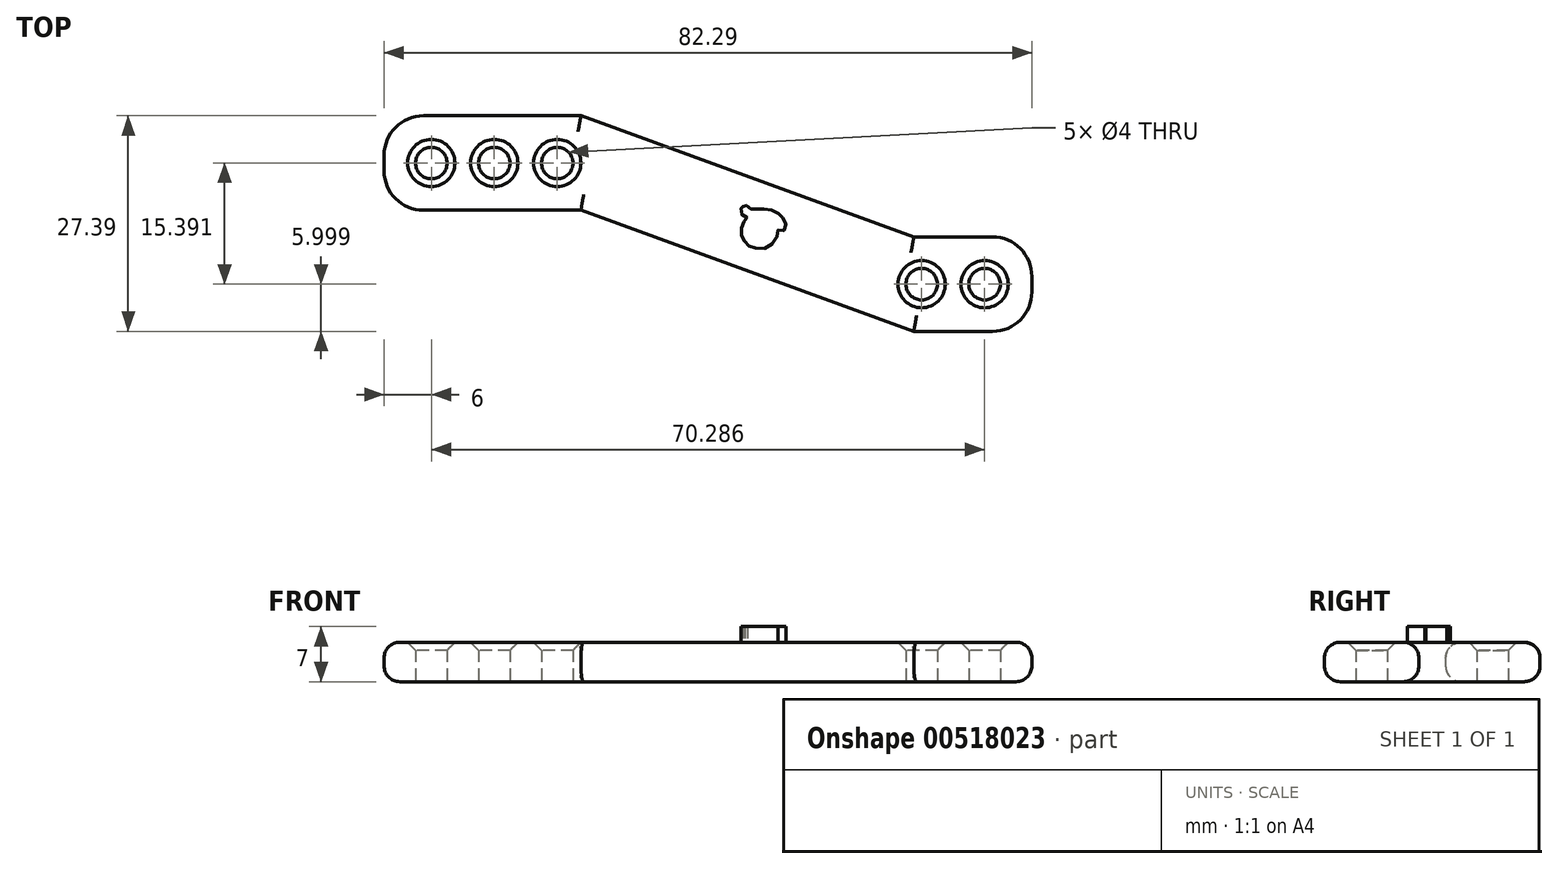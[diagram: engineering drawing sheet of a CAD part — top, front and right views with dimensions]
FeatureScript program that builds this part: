
annotation { "Feature Type Name" : "Feature", "Feature Type Description" : "" }
export const myFeature = defineFeature(function(context is Context, id is Id, definition is map)
    precondition{}
    {
        {
            var Q0;
            Q0=qCreatedBy(makeId("Top.planeOp"),FACE);
            var sketch = newSketch(context, id + "F0", { "sketchPlane" : qUnion([Q0])});
            skLineSegment(sketch, "E0.bottom", {"start": v(0, 0) * mm, "end": v(25, 0) * mm});
            skLineSegment(sketch, "E0.top", {"start": v(0, -12) * mm, "end": v(25, -12) * mm});
            skLineSegment(sketch, "E0.left", {"start": v(0, 0) * mm, "end": v(0, -12) * mm});
            skLineSegment(sketch, "E0.right", {"start": v(25, 0) * mm, "end": v(25, -12) * mm});
            skLineSegment(sketch, "E1", {"start": v(25, -12) * mm, "end": v(67.29, -27.4) * mm});
            skLineSegment(sketch, "E2", {"start": v(25, 0) * mm, "end": v(67.29, -15.4) * mm});
            skLineSegment(sketch, "E3", {"start": v(67.29, -15.4) * mm, "end": v(67.29, -27.4) * mm});
            skLineSegment(sketch, "E4.bottom", {"start": v(67.29, -27.4) * mm, "end": v(67.29, -27.4) * mm});
            skLineSegment(sketch, "E4.top", {"start": v(67.29, -15.4) * mm, "end": v(67.29, -15.4) * mm});
            skLineSegment(sketch, "E4.left", {"start": v(67.29, -27.4) * mm, "end": v(67.29, -15.4) * mm});
            skLineSegment(sketch, "E4.right", {"start": v(67.29, -27.4) * mm, "end": v(67.29, -15.4) * mm});
            skLineSegment(sketch, "E5.bottom", {"start": v(67.29, -27.4) * mm, "end": v(82.29, -27.4) * mm});
            skLineSegment(sketch, "E5.top", {"start": v(67.29, -15.4) * mm, "end": v(82.29, -15.4) * mm});
            skLineSegment(sketch, "E5.right", {"start": v(82.29, -27.4) * mm, "end": v(82.29, -15.4) * mm});
            skSolve(sketch);
        }
        {
            var Q0;
            Q0 = qSketchRegion(id + "F0", true);
            extrude(context, id + "F1", {"entities" : qUnion([Q0]), "depth" : 5 * mm, "offsetDistance" : 25 * mm});
        }
        {
            var Q0;
            Q0=qCreatedBy(makeId("Top.planeOp"),FACE);
            var sketch = newSketch(context, id + "F2", { "sketchPlane" : qUnion([Q0])});
            skCircle(sketch, "E6", {"center": v(6, -6) * mm, "radius": 2 * mm});
            skCircle(sketch, "E7", {"center": v(76.29, -21.4) * mm, "radius": 2 * mm});
            skCircle(sketch, "E8.1.0.0", {"center": v(14, -6) * mm, "radius": 2 * mm});
            skCircle(sketch, "E8.2.0.0", {"center": v(22, -6) * mm, "radius": 2 * mm});
            skLineSegment(sketch, "E8.direction1", {"start": v(6, -6) * mm, "end": v(14, -6) * mm, "construction": true});
            skCircle(sketch, "E9.1.0.0", {"center": v(68.29, -21.4) * mm, "radius": 2 * mm});
            skLineSegment(sketch, "E9.direction1", {"start": v(76.29, -21.4) * mm, "end": v(68.29, -21.4) * mm, "construction": true});
            skSolve(sketch);
        }
        {
            var Q0;
            Q0 = qSketchRegion(id + "F2", true);
            extrude(context, id + "F3", {"entities" : qUnion([Q0]), "operationType" : NewBodyOperationType.REMOVE, "endBound" : BoundingType.THROUGH_ALL, "depth" : 25 * mm, "offsetDistance" : 25 * mm});
        }
        {
            var Q0;
            Q0=makeQuery(id+"F1.opExtrude","CAP_EDGE",EDGE,{"disambiguationData":[OSD([sQuery(id+"F0.wireOp",EDGE,"E0.top")])],"isStart":false});
            var Q1;
            Q1=makeQuery(id+"F1.opExtrude","CAP_EDGE",EDGE,{"disambiguationData":[OSD([sQuery(id+"F0.wireOp",EDGE,"E2")])],"isStart":false});
            var Q2;
            Q2=makeQuery(id+"F1.opExtrude","CAP_EDGE",EDGE,{"disambiguationData":[OSD([sQuery(id+"F0.wireOp",EDGE,"E1")])],"isStart":false});
            var Q3;
            Q3=makeQuery(id+"F1.opExtrude","CAP_EDGE",EDGE,{"disambiguationData":[OSD([sQuery(id+"F0.wireOp",EDGE,"E5.top")])],"isStart":false});
            var Q4;
            Q4=makeQuery(id+"F1.opExtrude","CAP_EDGE",EDGE,{"disambiguationData":[OSD([sQuery(id+"F0.wireOp",EDGE,"E5.right")])],"isStart":false});
            var Q5;
            Q5=makeQuery(id+"F1.opExtrude","CAP_EDGE",EDGE,{"disambiguationData":[OSD([sQuery(id+"F0.wireOp",EDGE,"E5.bottom")])],"isStart":false});
            var Q6;
            Q6=makeQuery(id+"F1.opExtrude","CAP_EDGE",EDGE,{"disambiguationData":[OSD([sQuery(id+"F0.wireOp",EDGE,"E0.bottom")])],"isStart":false});
            var Q7;
            Q7=makeQuery(id+"F1.opExtrude","CAP_EDGE",EDGE,{"disambiguationData":[OSD([sQuery(id+"F0.wireOp",EDGE,"E0.left")])],"isStart":false});
            var Q8;
            Q8=makeQuery(id+"F1.opExtrude","CAP_EDGE",EDGE,{"disambiguationData":[OSD([sQuery(id+"F0.wireOp",EDGE,"E5.right")])],"isStart":true});
            var Q9;
            Q9=makeQuery(id+"F1.opExtrude","CAP_EDGE",EDGE,{"disambiguationData":[OSD([sQuery(id+"F0.wireOp",EDGE,"E5.top")])],"isStart":true});
            var Q10;
            Q10=makeQuery(id+"F1.opExtrude","CAP_EDGE",EDGE,{"disambiguationData":[OSD([sQuery(id+"F0.wireOp",EDGE,"E2")])],"isStart":true});
            var Q11;
            Q11=makeQuery(id+"F1.opExtrude","CAP_EDGE",EDGE,{"disambiguationData":[OSD([sQuery(id+"F0.wireOp",EDGE,"E0.bottom")])],"isStart":true});
            var Q12;
            Q12=makeQuery(id+"F1.opExtrude","CAP_EDGE",EDGE,{"disambiguationData":[OSD([sQuery(id+"F0.wireOp",EDGE,"E0.left")])],"isStart":true});
            var Q13;
            Q13=makeQuery(id+"F1.opExtrude","CAP_EDGE",EDGE,{"disambiguationData":[OSD([sQuery(id+"F0.wireOp",EDGE,"E0.top")])],"isStart":true});
            var Q14;
            Q14=makeQuery(id+"F1.opExtrude","CAP_EDGE",EDGE,{"disambiguationData":[OSD([sQuery(id+"F0.wireOp",EDGE,"E1")])],"isStart":true});
            var Q15;
            Q15=makeQuery(id+"F1.opExtrude","CAP_EDGE",EDGE,{"disambiguationData":[OSD([sQuery(id+"F0.wireOp",EDGE,"E5.bottom")])],"isStart":true});
            fillet(context, id + "F4", {"entities" : qUnion([Q0, Q1, Q2, Q3, Q4, Q5, Q6, Q7, Q8, Q9, Q10, Q11, Q12, Q13, Q14, Q15]), "radius" : 2 * mm, "tangentPropagation" : true, "allowEdgeOverflow" : false});
        }
        {
            var Q0;
            Q0=makeQuery(id+"F1.opExtrude","SWEPT_EDGE",EDGE,{"disambiguationData":[OSD([sQuery(id+"F0.wireOp",EDGE,"E0.top"),sQuery(id+"F0.wireOp",EDGE,"E0.left")])]});
            var Q1;
            Q1=makeQuery(id+"F1.opExtrude","SWEPT_EDGE",EDGE,{"disambiguationData":[OSD([sQuery(id+"F0.wireOp",EDGE,"E0.bottom"),sQuery(id+"F0.wireOp",EDGE,"E0.left")])]});
            var Q2;
            Q2=makeQuery(id+"F1.opExtrude","SWEPT_EDGE",EDGE,{"disambiguationData":[OSD([sQuery(id+"F0.wireOp",EDGE,"E5.top"),sQuery(id+"F0.wireOp",EDGE,"E5.right")])]});
            var Q3;
            Q3=makeQuery(id+"F1.opExtrude","SWEPT_EDGE",EDGE,{"disambiguationData":[OSD([sQuery(id+"F0.wireOp",EDGE,"E5.bottom"),sQuery(id+"F0.wireOp",EDGE,"E5.right")])]});
            fillet(context, id + "F5", {"entities" : qUnion([Q0, Q1, Q2, Q3]), "radius" : 5 * mm, "tangentPropagation" : true, "allowEdgeOverflow" : false});
        }
        {
            var Q0;
            Q0=makeQuery(id+"F3.boolean.opBoolean","INTERSECT",EDGE,{"derivedFrom":[makeQuery(id+"F1.opExtrude","CAP_FACE",FACE,{"disambiguationData":[OSD([sQuery(id+"F0.wireOp",EDGE,"E0.bottom"),sQuery(id+"F0.wireOp",EDGE,"E0.top"),sQuery(id+"F0.wireOp",EDGE,"E0.left"),sQuery(id+"F0.wireOp",EDGE,"E1"),sQuery(id+"F0.wireOp",EDGE,"E2"),sQuery(id+"F0.wireOp",EDGE,"E5.bottom"),sQuery(id+"F0.wireOp",EDGE,"E5.top"),sQuery(id+"F0.wireOp",EDGE,"E5.right")])],"isStart":false}),makeQuery(id+"F3.opExtrude","SWEPT_FACE",FACE,{"disambiguationData":[OSD([sQuery(id+"F2.wireOp",EDGE,"E9.1.0.0")])]})]});
            var Q1;
            Q1=makeQuery(id+"F3.boolean.opBoolean","INTERSECT",EDGE,{"derivedFrom":[makeQuery(id+"F1.opExtrude","CAP_FACE",FACE,{"disambiguationData":[OSD([sQuery(id+"F0.wireOp",EDGE,"E0.bottom"),sQuery(id+"F0.wireOp",EDGE,"E0.top"),sQuery(id+"F0.wireOp",EDGE,"E0.left"),sQuery(id+"F0.wireOp",EDGE,"E1"),sQuery(id+"F0.wireOp",EDGE,"E2"),sQuery(id+"F0.wireOp",EDGE,"E5.bottom"),sQuery(id+"F0.wireOp",EDGE,"E5.top"),sQuery(id+"F0.wireOp",EDGE,"E5.right")])],"isStart":false}),makeQuery(id+"F3.opExtrude","SWEPT_FACE",FACE,{"disambiguationData":[OSD([sQuery(id+"F2.wireOp",EDGE,"E7")])]})]});
            var Q2;
            Q2=makeQuery(id+"F3.boolean.opBoolean","INTERSECT",EDGE,{"derivedFrom":[makeQuery(id+"F1.opExtrude","CAP_FACE",FACE,{"disambiguationData":[OSD([sQuery(id+"F0.wireOp",EDGE,"E0.bottom"),sQuery(id+"F0.wireOp",EDGE,"E0.top"),sQuery(id+"F0.wireOp",EDGE,"E0.left"),sQuery(id+"F0.wireOp",EDGE,"E1"),sQuery(id+"F0.wireOp",EDGE,"E2"),sQuery(id+"F0.wireOp",EDGE,"E5.bottom"),sQuery(id+"F0.wireOp",EDGE,"E5.top"),sQuery(id+"F0.wireOp",EDGE,"E5.right")])],"isStart":false}),makeQuery(id+"F3.opExtrude","SWEPT_FACE",FACE,{"disambiguationData":[OSD([sQuery(id+"F2.wireOp",EDGE,"E8.2.0.0")])]})]});
            var Q3;
            Q3=makeQuery(id+"F3.boolean.opBoolean","INTERSECT",EDGE,{"derivedFrom":[makeQuery(id+"F1.opExtrude","CAP_FACE",FACE,{"disambiguationData":[OSD([sQuery(id+"F0.wireOp",EDGE,"E0.bottom"),sQuery(id+"F0.wireOp",EDGE,"E0.top"),sQuery(id+"F0.wireOp",EDGE,"E0.left"),sQuery(id+"F0.wireOp",EDGE,"E1"),sQuery(id+"F0.wireOp",EDGE,"E2"),sQuery(id+"F0.wireOp",EDGE,"E5.bottom"),sQuery(id+"F0.wireOp",EDGE,"E5.top"),sQuery(id+"F0.wireOp",EDGE,"E5.right")])],"isStart":false}),makeQuery(id+"F3.opExtrude","SWEPT_FACE",FACE,{"disambiguationData":[OSD([sQuery(id+"F2.wireOp",EDGE,"E8.1.0.0")])]})]});
            var Q4;
            Q4=makeQuery(id+"F3.boolean.opBoolean","INTERSECT",EDGE,{"derivedFrom":[makeQuery(id+"F1.opExtrude","CAP_FACE",FACE,{"disambiguationData":[OSD([sQuery(id+"F0.wireOp",EDGE,"E0.bottom"),sQuery(id+"F0.wireOp",EDGE,"E0.top"),sQuery(id+"F0.wireOp",EDGE,"E0.left"),sQuery(id+"F0.wireOp",EDGE,"E1"),sQuery(id+"F0.wireOp",EDGE,"E2"),sQuery(id+"F0.wireOp",EDGE,"E5.bottom"),sQuery(id+"F0.wireOp",EDGE,"E5.top"),sQuery(id+"F0.wireOp",EDGE,"E5.right")])],"isStart":false}),makeQuery(id+"F3.opExtrude","SWEPT_FACE",FACE,{"disambiguationData":[OSD([sQuery(id+"F2.wireOp",EDGE,"E6")])]})]});
            chamfer(context, id + "F6", {"entities" : qUnion([Q0, Q1, Q2, Q3, Q4]), "width" : 1 * mm, "tangentPropagation" : true});
        }
        {
            var Q0;
            Q0=qCreatedBy(makeId("Top.planeOp"),FACE);
            var sketch = newSketch(context, id + "F7", { "sketchPlane" : qUnion([Q0])});
            skPoint(sketch, "E10.27.internal.snap0", {"position": v(49, -10.86) * mm});
            skFitSpline(sketch, "E10", {"points": [v(49.38, -16.1) * mm, v(49.43, -16.04) * mm, v(49.48, -15.98) * mm, v(49.54, -15.91) * mm, v(49.61, -15.83) * mm, v(49.67, -15.72) * mm, v(49.8, -15.56) * mm, v(49.9, -15.4) * mm, v(49.95, -15.25) * mm, v(50, -15.12) * mm, v(50.1, -14.62) * mm, v(50.08, -14.39) * mm, v(50.22, -14.34) * mm, v(50.34, -14.42) * mm, v(50.44, -14.45) * mm, v(50.68, -14.44) * mm, v(50.86, -14.34) * mm, v(50.98, -14.1) * mm, v(51.1, -13.66) * mm, v(50.97, -13.08) * mm, v(50.73, -12.75) * mm, v(50.4, -12.45) * mm, v(50.07, -12.22) * mm, v(49.92, -12.14) * mm, v(49.64, -11.97) * mm, v(49.47, -11.94) * mm, v(49.3, -11.85) * mm, v(49, -11.73) * mm, v(48.65, -11.7) * mm, v(48.39, -11.7) * mm, v(48.14, -11.7) * mm, v(47.81, -11.66) * mm, v(47.66, -11.67) * mm, v(47.28, -11.66) * mm, v(47.14, -11.7) * mm, v(46.88, -11.71) * mm, v(46.64, -11.65) * mm, v(46.43, -11.56) * mm, v(46.28, -11.47) * mm, v(46.2, -11.34) * mm, v(46.1, -11.2) * mm, v(46.04, -11.24) * mm, v(45.98, -11.28) * mm, v(45.96, -11.38) * mm, v(45.93, -11.48) * mm, v(45.93, -11.5) * mm], "startDerivative": vector(3.06, 4.52) * mm, "endDerivative": vector(0.44, -3) * mm});
            skPoint(sketch, "E11.47.internal.snap0", {"position": v(46.6, -17.44) * mm});
            skFitSpline(sketch, "E11", {"points": [v(45.85, -11.49) * mm, v(45.76, -11.41) * mm, v(45.73, -11.37) * mm, v(45.71, -11.34) * mm, v(45.67, -11.42) * mm, v(45.66, -11.51) * mm, v(45.64, -11.6) * mm, v(45.64, -11.71) * mm, v(45.64, -11.73) * mm, v(45.64, -11.82) * mm, v(45.58, -11.8) * mm, v(45.54, -11.7) * mm, v(45.52, -11.65) * mm, v(45.5, -11.64) * mm, v(45.48, -11.82) * mm, v(45.46, -11.98) * mm, v(45.49, -12.18) * mm, v(45.52, -12.33) * mm, v(45.64, -12.45) * mm, v(45.78, -12.55) * mm, v(45.88, -12.62) * mm, v(46.04, -12.68) * mm, v(46.18, -12.72) * mm, v(46.13, -12.78) * mm, v(46.04, -12.96) * mm, v(45.96, -13.02) * mm, v(45.9, -13.1) * mm, v(45.77, -13.24) * mm, v(45.77, -13.35) * mm, v(45.71, -13.47) * mm, v(45.66, -13.6) * mm, v(45.58, -13.77) * mm, v(45.53, -13.88) * mm, v(45.5, -14) * mm, v(45.47, -14.1) * mm, v(45.46, -14.26) * mm, v(45.46, -14.33) * mm, v(45.47, -14.6) * mm, v(45.53, -14.77) * mm, v(45.53, -14.96) * mm, v(45.57, -15.1) * mm, v(45.6, -15.34) * mm, v(45.68, -15.56) * mm, v(45.8, -15.75) * mm, v(45.98, -16) * mm, v(46.18, -16.15) * mm, v(46.45, -16.32) * mm, v(46.6, -16.45) * mm, v(47, -16.55) * mm, v(47.14, -16.6) * mm, v(47.44, -16.67) * mm, v(47.69, -16.74) * mm, v(47.98, -16.76) * mm, v(48.34, -16.76) * mm, v(48.5, -16.65) * mm, v(48.77, -16.6) * mm, v(48.88, -16.5) * mm, v(49.1, -16.37) * mm, v(49.2, -16.26) * mm, v(49.32, -16.2) * mm, v(49.38, -16.1) * mm, v(49.48, -15.98) * mm], "startDerivative": vector(-7.45, 5.74) * mm, "endDerivative": vector(6.63, 7.35) * mm});
            skSolve(sketch);
        }
        {
            var Q0;
            Q0 = qSketchRegion(id + "F7", true);
            extrude(context, id + "F8", {"entities" : qUnion([Q0]), "operationType" : NewBodyOperationType.ADD, "depth" : 5 * mm, "offsetDistance" : 25 * mm});
        }
        {
            var Q0;
            Q0=makeQuery(id+"F1.opExtrude","CAP_FACE",FACE,{"disambiguationData":[OSD([sQuery(id+"F0.wireOp",EDGE,"E0.bottom"),sQuery(id+"F0.wireOp",EDGE,"E0.top"),sQuery(id+"F0.wireOp",EDGE,"E0.left"),sQuery(id+"F0.wireOp",EDGE,"E1"),sQuery(id+"F0.wireOp",EDGE,"E2"),sQuery(id+"F0.wireOp",EDGE,"E5.bottom"),sQuery(id+"F0.wireOp",EDGE,"E5.top"),sQuery(id+"F0.wireOp",EDGE,"E5.right")])],"isStart":false});
            var sketch = newSketch(context, id + "F9", { "sketchPlane" : qUnion([Q0])});
            skFitSpline(sketch, "E12", {"points": [v(47.18, -16.78) * mm, v(47.8, -16.85) * mm, v(48.32, -16.85) * mm, v(48.7, -16.78) * mm, v(49.22, -16.33) * mm, v(49.65, -15.84) * mm, v(49.9, -15.43) * mm, v(50.02, -15.03) * mm, v(50.03, -14.74) * mm, v(50.03, -14.53) * mm, v(50.27, -14.54) * mm, v(50.45, -14.6) * mm, v(50.79, -14.6) * mm, v(50.9, -14.4) * mm, v(51.02, -14) * mm, v(51.04, -13.6) * mm, v(50.85, -13.2) * mm, v(50.64, -12.94) * mm, v(50.47, -12.76) * mm, v(50.3, -12.6) * mm, v(50.12, -12.42) * mm, v(49.83, -12.22) * mm, v(49.4, -12.04) * mm, v(49.05, -11.94) * mm, v(48.65, -11.86) * mm, v(48.23, -11.84) * mm, v(47.75, -11.82) * mm, v(47.4, -11.82) * mm, v(47.2, -11.86) * mm, v(46.93, -11.87) * mm, v(46.71, -11.84) * mm, v(46.53, -11.8) * mm, v(46.38, -11.69) * mm, v(46.16, -11.54) * mm, v(46, -11.37) * mm, v(45.88, -11.42) * mm, v(45.86, -11.64) * mm, v(45.64, -11.5) * mm, v(45.6, -11.64) * mm, v(45.58, -11.86) * mm, v(45.56, -11.94) * mm, v(45.38, -11.77) * mm, v(45.38, -11.99) * mm, v(45.38, -12.24) * mm, v(45.43, -12.54) * mm, v(45.61, -12.66) * mm, v(45.86, -12.84) * mm, v(46.05, -12.9) * mm, v(46.15, -12.92) * mm, v(45.96, -13.1) * mm, v(45.8, -13.27) * mm, v(45.64, -13.56) * mm, v(45.53, -13.84) * mm, v(45.44, -14.1) * mm, v(45.33, -14.54) * mm, v(45.4, -14.94) * mm, v(45.44, -15.24) * mm, v(45.53, -15.48) * mm, v(45.64, -15.64) * mm, v(45.8, -15.96) * mm, v(46.01, -16.23) * mm, v(46.28, -16.5) * mm, v(46.51, -16.68) * mm, v(46.85, -16.75) * mm, v(47.18, -16.78) * mm]});
            skSolve(sketch);
        }
        {
            var Q0;
            Q0=makeQuery(id+"F9.imprint","IMPRINT",FACE,{"disambiguationData":[TD([[makeQuery(id+"F9.imprint","IMPRINT",EDGE,{"derivedFrom":sQuery(id+"F9.wireOp",EDGE,"E12")}),1.0]])]});
            extrude(context, id + "F10", {"entities" : qUnion([Q0]), "operationType" : NewBodyOperationType.ADD, "depth" : 2 * mm, "offsetDistance" : 25 * mm});
        }
    });
